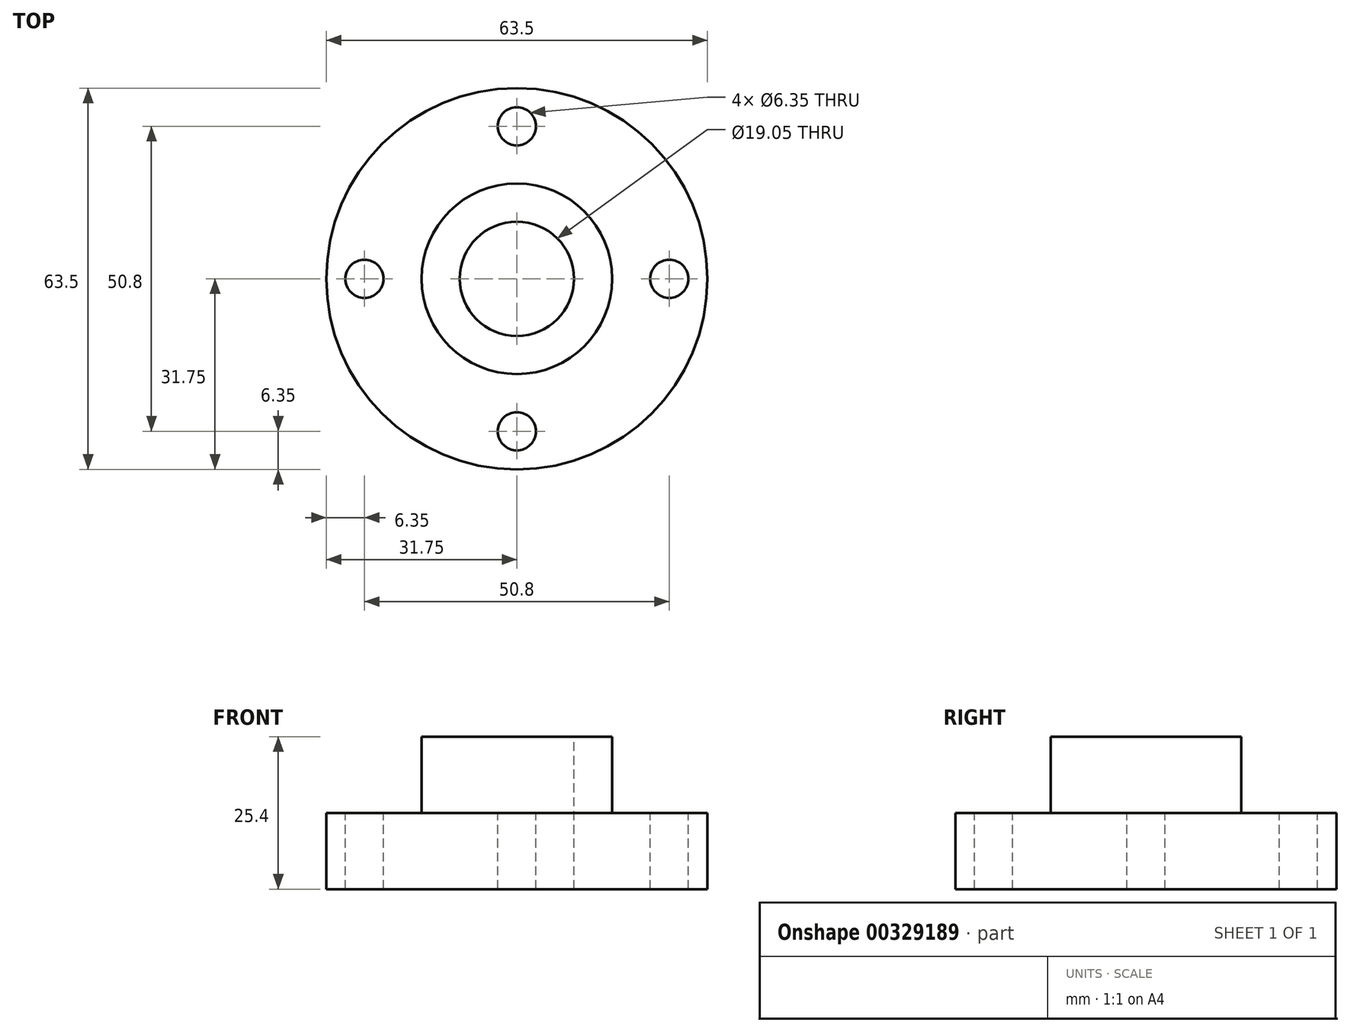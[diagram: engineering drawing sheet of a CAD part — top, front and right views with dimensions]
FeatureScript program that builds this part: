
annotation { "Feature Type Name" : "Feature", "Feature Type Description" : "" }
export const myFeature = defineFeature(function(context is Context, id is Id, definition is map)
    precondition{}
    {
        {
            var Q0;
            Q0=qCreatedBy(makeId("Top.planeOp"),FACE);
            var sketch = newSketch(context, id + "F0", { "sketchPlane" : qUnion([Q0])});
            skCircle(sketch, "E0", {"center": v(0, 0) * mm, "radius": 31.75 * mm});
            skSolve(sketch);
        }
        {
            var Q0;
            Q0 = qSketchRegion(id + "F0", true);
            extrude(context, id + "F1", {"entities" : qUnion([Q0]), "depth" : 12.7 * mm});
        }
        {
            var Q0;
            Q0=makeQuery(id+"F1.opExtrude","CAP_FACE",FACE,{"disambiguationData":[OSD([sQuery(id+"F0.wireOp",EDGE,"E0")])],"isStart":false});
            var sketch = newSketch(context, id + "F2", { "sketchPlane" : qUnion([Q0])});
            skCircle(sketch, "E1", {"center": v(0, 0) * mm, "radius": 15.88 * mm});
            skSolve(sketch);
        }
        {
            var Q0;
            Q0 = qSketchRegion(id + "F2", true);
            extrude(context, id + "F3", {"entities" : qUnion([Q0]), "operationType" : NewBodyOperationType.ADD, "depth" : 12.7 * mm});
        }
        {
            var Q0;
            Q0=makeQuery(id+"F3.opExtrude","CAP_FACE",FACE,{"disambiguationData":[OSD([sQuery(id+"F2.wireOp",EDGE,"E1")])],"isStart":false});
            var sketch = newSketch(context, id + "F4", { "sketchPlane" : qUnion([Q0])});
            skCircle(sketch, "E2", {"center": v(0, 0) * mm, "radius": 9.53 * mm});
            skCircle(sketch, "E3", {"center": v(0, 25.4) * mm, "radius": 3.18 * mm});
            skCircle(sketch, "E4", {"center": v(0, -25.4) * mm, "radius": 3.18 * mm});
            skCircle(sketch, "E5", {"center": v(-25.4, 0) * mm, "radius": 3.18 * mm});
            skCircle(sketch, "E6", {"center": v(25.4, 0) * mm, "radius": 3.18 * mm});
            skSolve(sketch);
        }
        {
            var Q0;
            Q0 = qSketchRegion(id + "F4", true);
            extrude(context, id + "F5", {"entities" : qUnion([Q0]), "operationType" : NewBodyOperationType.REMOVE, "endBound" : BoundingType.THROUGH_ALL, "oppositeDirection" : true, "depth" : 25.4 * mm});
        }
    });
